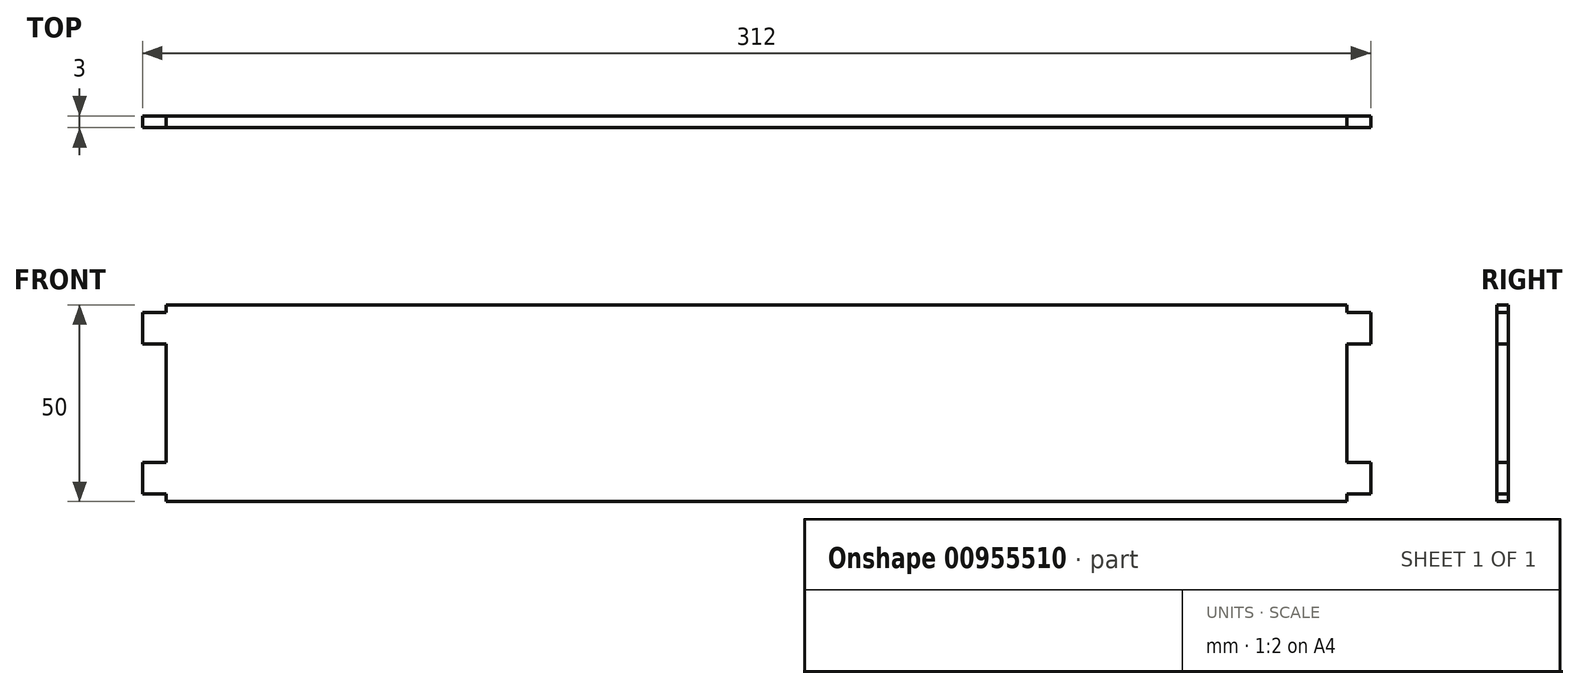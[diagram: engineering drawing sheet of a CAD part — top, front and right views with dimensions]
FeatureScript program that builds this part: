
annotation { "Feature Type Name" : "Feature", "Feature Type Description" : "" }
export const myFeature = defineFeature(function(context is Context, id is Id, definition is map)
    precondition{}
    {
        {
            var Q0;
            Q0=qCreatedBy(makeId("Front.planeOp"),FACE);
            var sketch = newSketch(context, id + "F0", { "sketchPlane" : qUnion([Q0])});
            skLineSegment(sketch, "E0.bottom", {"start": v(-59.97, 1.46) * mm, "end": v(240.03, 1.46) * mm});
            skLineSegment(sketch, "E0.top", {"start": v(-59.97, 51.46) * mm, "end": v(240.03, 51.46) * mm});
            skLineSegment(sketch, "E0.left", {"start": v(-59.97, 1.46) * mm, "end": v(-59.97, 3.46) * mm});
            skLineSegment(sketch, "E0.right", {"start": v(240.03, 1.46) * mm, "end": v(240.03, 3.46) * mm});
            skLineSegment(sketch, "E1.bottom", {"start": v(-59.97, 49.46) * mm, "end": v(-65.97, 49.46) * mm});
            skLineSegment(sketch, "E1.top", {"start": v(-59.97, 41.46) * mm, "end": v(-65.97, 41.46) * mm});
            skLineSegment(sketch, "E1.right", {"start": v(-65.97, 49.46) * mm, "end": v(-65.97, 41.46) * mm});
            skLineSegment(sketch, "E2.0.1.0", {"start": v(-59.97, 11.46) * mm, "end": v(-65.97, 11.46) * mm});
            skLineSegment(sketch, "E2.0.1.1", {"start": v(-65.97, 11.46) * mm, "end": v(-65.97, 3.46) * mm});
            skLineSegment(sketch, "E2.0.1.2", {"start": v(-59.97, 3.46) * mm, "end": v(-65.97, 3.46) * mm});
            skLineSegment(sketch, "E2.1.0.0", {"start": v(246.03, 49.46) * mm, "end": v(240.03, 49.46) * mm});
            skLineSegment(sketch, "E2.1.0.2", {"start": v(246.03, 41.46) * mm, "end": v(240.03, 41.46) * mm});
            skLineSegment(sketch, "E2.1.0.3", {"start": v(246.03, 49.46) * mm, "end": v(246.03, 41.46) * mm});
            skLineSegment(sketch, "E2.1.1.0", {"start": v(246.03, 11.46) * mm, "end": v(240.03, 11.46) * mm});
            skLineSegment(sketch, "E2.1.1.2", {"start": v(246.03, 3.46) * mm, "end": v(240.03, 3.46) * mm});
            skLineSegment(sketch, "E2.1.1.3", {"start": v(246.03, 11.46) * mm, "end": v(246.03, 3.46) * mm});
            skLineSegment(sketch, "E2.direction1", {"start": v(-65.97, 49.46) * mm, "end": v(240.03, 49.46) * mm, "construction": true});
            skLineSegment(sketch, "E2.direction2", {"start": v(-65.97, 49.46) * mm, "end": v(-65.97, 11.46) * mm, "construction": true});
            skLineSegment(sketch, "E3.trimOffspring", {"start": v(-59.97, 49.46) * mm, "end": v(-59.97, 51.46) * mm});
            skLineSegment(sketch, "E4.trimOffspring", {"start": v(-59.97, 11.46) * mm, "end": v(-59.97, 41.46) * mm});
            skLineSegment(sketch, "E5.trimOffspring", {"start": v(240.03, 49.46) * mm, "end": v(240.03, 51.46) * mm});
            skLineSegment(sketch, "E6.trimOffspring", {"start": v(240.03, 11.46) * mm, "end": v(240.03, 41.46) * mm});
            skSolve(sketch);
        }
        {
            var Q0;
            Q0=qSketchRegion(id+"F0",true);
            extrude(context, id + "F1", {"entities" : qUnion([Q0]), "depth" : 3 * mm, "offsetDistance" : 25 * mm});
        }
    });
